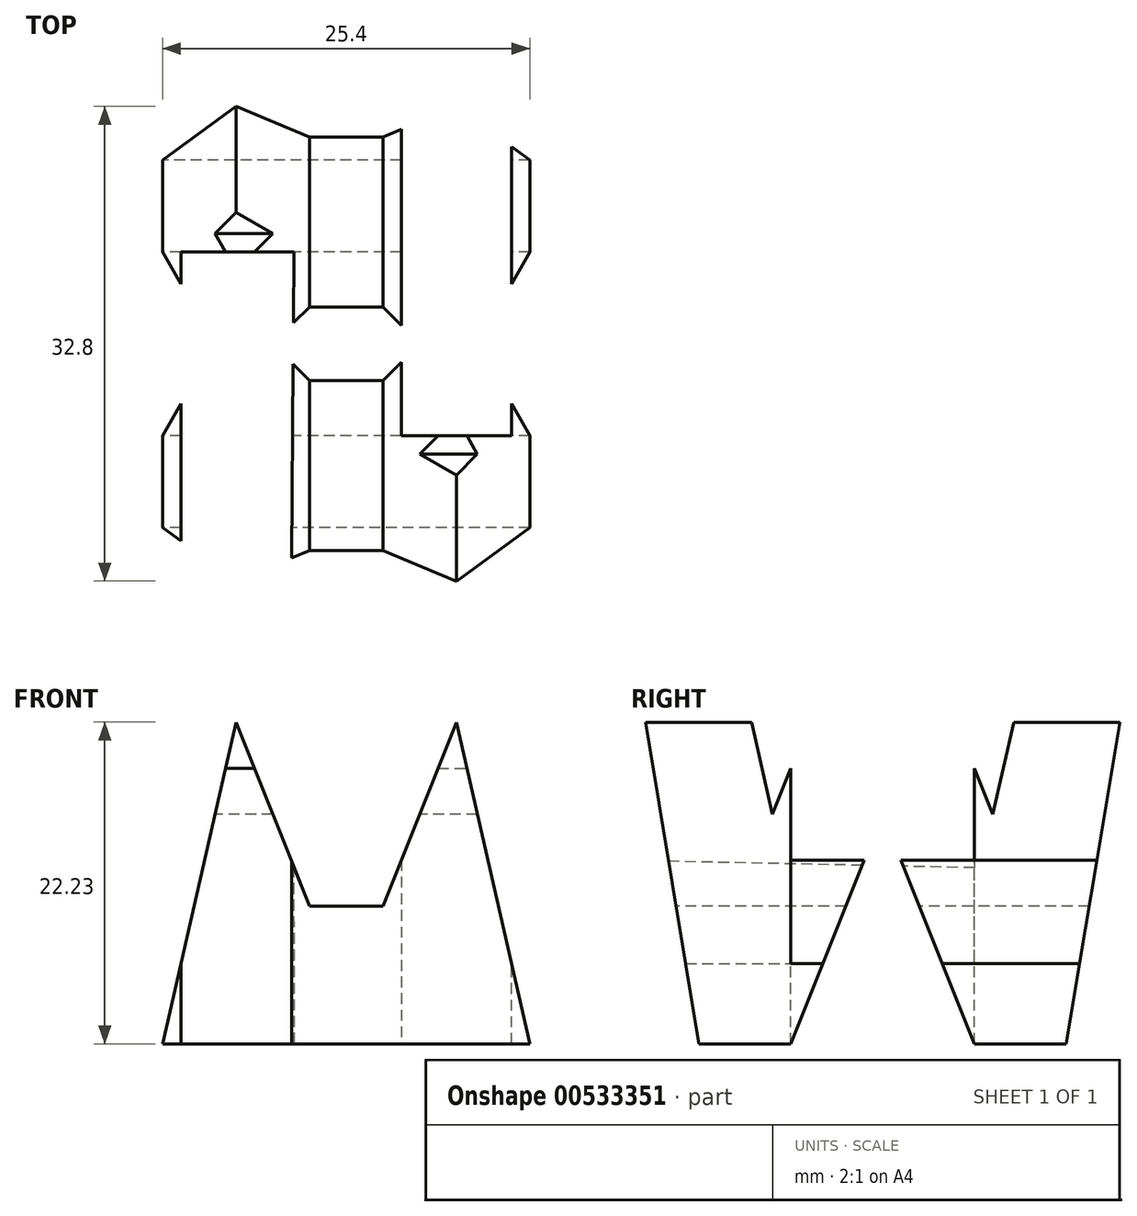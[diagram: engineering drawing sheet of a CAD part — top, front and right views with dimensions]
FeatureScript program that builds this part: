
annotation { "Feature Type Name" : "Feature", "Feature Type Description" : "" }
export const myFeature = defineFeature(function(context is Context, id is Id, definition is map)
    precondition{}
    {
        {
            var Q0;
            Q0=qCreatedBy(makeId("Front.planeOp"),FACE);
            var sketch = newSketch(context, id + "F0", { "sketchPlane" : qUnion([Q0])});
            skLineSegment(sketch, "E0", {"start": v(0, 0) * mm, "end": v(-38.1, 0) * mm});
            skLineSegment(sketch, "E1", {"start": v(-38.1, 0) * mm, "end": v(-38.1, -38.1) * mm});
            skLineSegment(sketch, "E2", {"start": v(-38.1, -38.1) * mm, "end": v(0, -38.1) * mm});
            skLineSegment(sketch, "E3", {"start": v(0, -38.1) * mm, "end": v(0, 0) * mm});
            skSolve(sketch);
        }
        {
            var Q0;
            Q0 = qSketchRegion(id + "F0", true);
            extrude(context, id + "F1", {"entities" : qUnion([Q0]), "depth" : 38.1 * mm, "offsetDistance" : 25.4 * mm});
        }
        {
            var Q0;
            Q0=qCreatedBy(makeId("Front.planeOp"),FACE);
            cPlane(context, id + "F2", {"entities" : qUnion([Q0]), "cplaneType" : CPlaneType.OFFSET, "offset" : 38.1 * mm, "width" : 152.4 * mm, "height" : 152.4 * mm});
        }
        {
            var Q0;
            Q0=qCreatedBy(makeId("Right.planeOp"),FACE);
            cPlane(context, id + "F3", {"entities" : qUnion([Q0]), "cplaneType" : CPlaneType.OFFSET, "offset" : 38.1 * mm, "oppositeDirection" : true, "width" : 152.4 * mm, "height" : 152.4 * mm});
        }
        {
            var Q0;
            Q0=qCreatedBy(id+"F3.planeOp",FACE);
            var sketch = newSketch(context, id + "F4", { "sketchPlane" : qUnion([Q0])});
            skLineSegment(sketch, "E4", {"start": v(0, 0) * mm, "end": v(-38.1, 0) * mm});
            skLineSegment(sketch, "E5", {"start": v(-38.1, 0) * mm, "end": v(-38.1, -38.1) * mm});
            skLineSegment(sketch, "E6", {"start": v(-38.1, -38.1) * mm, "end": v(0, -38.1) * mm});
            skLineSegment(sketch, "E7", {"start": v(0, -38.1) * mm, "end": v(0, 0) * mm});
            skLineSegment(sketch, "E8", {"start": v(-38.1, 0) * mm, "end": v(-31.75, -38.1) * mm});
            skLineSegment(sketch, "E9", {"start": v(-31.75, -38.1) * mm, "end": v(-25.4, -38.1) * mm});
            skLineSegment(sketch, "E10", {"start": v(-25.4, -38.1) * mm, "end": v(-19.05, -22.23) * mm});
            skLineSegment(sketch, "E11", {"start": v(-19.05, -22.23) * mm, "end": v(-12.7, -38.1) * mm});
            skLineSegment(sketch, "E12", {"start": v(-12.7, -38.1) * mm, "end": v(-6.35, -38.1) * mm});
            skLineSegment(sketch, "E13", {"start": v(-6.35, -38.1) * mm, "end": v(0, 0) * mm});
            skLineSegment(sketch, "E14", {"start": v(-31.75, 0) * mm, "end": v(-26.67, -22.23) * mm});
            skLineSegment(sketch, "E15", {"start": v(-26.67, -22.23) * mm, "end": v(-21.59, -9.52) * mm});
            skLineSegment(sketch, "E16", {"start": v(-21.59, -9.52) * mm, "end": v(-16.5, -9.52) * mm});
            skLineSegment(sketch, "E17", {"start": v(-16.5, -9.52) * mm, "end": v(-11.43, -22.23) * mm});
            skLineSegment(sketch, "E18", {"start": v(-11.43, -22.23) * mm, "end": v(-6.35, 0) * mm});
            skSolve(sketch);
        }
        {
            var Q0;
            {var subQ0=sQuery(id+"F4.wireOp",EDGE,"E10");Q0=makeQuery(id+"F4.imprint","IMPRINT",FACE,{"disambiguationData":[TD([[makeQuery(id+"F4.imprint","IMPRINT",EDGE,{"derivedFrom":subQ0}),-1.0]])]});}
            var Q1;
            {var subQ0=sQuery(id+"F4.wireOp",EDGE,"E14");Q1=makeQuery(id+"F4.imprint","IMPRINT",FACE,{"disambiguationData":[TD([[makeQuery(id+"F4.imprint","IMPRINT",EDGE,{"derivedFrom":subQ0}),1.0]])]});}
            var Q2;
            {var subQ0=sQuery(id+"F4.wireOp",EDGE,"E5");Q2=makeQuery(id+"F4.imprint","IMPRINT",FACE,{"disambiguationData":[TD([[makeQuery(id+"F4.imprint","IMPRINT",EDGE,{"derivedFrom":subQ0}),1.0]])]});}
            var Q3;
            {var subQ0=sQuery(id+"F4.wireOp",EDGE,"E7");Q3=makeQuery(id+"F4.imprint","IMPRINT",FACE,{"disambiguationData":[TD([[makeQuery(id+"F4.imprint","IMPRINT",EDGE,{"derivedFrom":subQ0}),1.0]])]});}
            extrude(context, id + "F5", {"entities" : qUnion([Q0, Q1, Q2, Q3]), "operationType" : NewBodyOperationType.REMOVE, "depth" : 38.1 * mm, "offsetDistance" : 25.4 * mm});
        }
        {
            var Q0;
            Q0=qCreatedBy(id+"F2.planeOp",FACE);
            var sketch = newSketch(context, id + "F6", { "sketchPlane" : qUnion([Q0])});
            skLineSegment(sketch, "E19", {"start": v(-38.1, -38.1) * mm, "end": v(-38.1, 0) * mm});
            skLineSegment(sketch, "E20", {"start": v(-38.1, 0) * mm, "end": v(0, 0) * mm});
            skLineSegment(sketch, "E21", {"start": v(0, 0) * mm, "end": v(0, -38.1) * mm});
            skLineSegment(sketch, "E22", {"start": v(0, -38.1) * mm, "end": v(-38.1, -38.1) * mm});
            skLineSegment(sketch, "E23", {"start": v(-38.1, -38.1) * mm, "end": v(-31.75, 0) * mm});
            skLineSegment(sketch, "E24", {"start": v(-31.75, 0) * mm, "end": v(-25.4, 0) * mm});
            skLineSegment(sketch, "E25", {"start": v(-25.4, 0) * mm, "end": v(-19.05, -15.88) * mm});
            skLineSegment(sketch, "E26", {"start": v(-19.05, -15.88) * mm, "end": v(-12.7, 0) * mm});
            skLineSegment(sketch, "E27", {"start": v(-12.7, 0) * mm, "end": v(-6.35, 0) * mm});
            skLineSegment(sketch, "E28", {"start": v(-6.35, 0) * mm, "end": v(0, -38.1) * mm});
            skLineSegment(sketch, "E29", {"start": v(-38.1, -38.1) * mm, "end": v(-31.75, -38.1) * mm});
            skLineSegment(sketch, "E30", {"start": v(-31.75, -38.1) * mm, "end": v(-38.1, -38.1) * mm});
            skLineSegment(sketch, "E31", {"start": v(-31.75, -38.1) * mm, "end": v(-26.67, -15.88) * mm});
            skLineSegment(sketch, "E32", {"start": v(-6.35, -38.1) * mm, "end": v(0, -38.1) * mm});
            skLineSegment(sketch, "E33", {"start": v(-26.67, -15.88) * mm, "end": v(-21.6, -28.58) * mm});
            skLineSegment(sketch, "E34", {"start": v(-11.43, -15.88) * mm, "end": v(-16.51, -28.58) * mm});
            skLineSegment(sketch, "E35", {"start": v(-16.51, -28.58) * mm, "end": v(-21.59, -28.58) * mm});
            skLineSegment(sketch, "E36", {"start": v(-11.43, -15.88) * mm, "end": v(-6.35, -38.1) * mm});
            skSolve(sketch);
        }
        {
            var Q0;
            Q0=makeQuery(id+"F6.imprint","IMPRINT",FACE,{"disambiguationData":[TD([[makeQuery(id+"F6.imprint","IMPRINT",EDGE,{"derivedFrom":sQuery(id+"F6.wireOp",EDGE,"E22")}),-1.0]])]});
            var Q1;
            {var subQ0=sQuery(id+"F6.wireOp",EDGE,"E25");Q1=makeQuery(id+"F6.imprint","IMPRINT",FACE,{"disambiguationData":[TD([[makeQuery(id+"F6.imprint","IMPRINT",EDGE,{"derivedFrom":subQ0}),1.0]])]});}
            var Q2;
            {var subQ0=sQuery(id+"F6.wireOp",EDGE,"E21");Q2=makeQuery(id+"F6.imprint","IMPRINT",FACE,{"disambiguationData":[TD([[makeQuery(id+"F6.imprint","IMPRINT",EDGE,{"derivedFrom":subQ0}),-1.0]])]});}
            var Q3;
            {var subQ0=sQuery(id+"F6.wireOp",EDGE,"E19");Q3=makeQuery(id+"F6.imprint","IMPRINT",FACE,{"disambiguationData":[TD([[makeQuery(id+"F6.imprint","IMPRINT",EDGE,{"derivedFrom":subQ0}),-1.0]])]});}
            extrude(context, id + "F7", {"entities" : qUnion([Q0, Q1, Q2, Q3]), "operationType" : NewBodyOperationType.REMOVE, "oppositeDirection" : true, "depth" : 38.1 * mm, "offsetDistance" : 25.4 * mm});
        }
        {
            var Q0;
            Q0=qCreatedBy(makeId("Top.planeOp"),FACE);
            var sketch = newSketch(context, id + "F8", { "sketchPlane" : qUnion([Q0])});
            skLineSegment(sketch, "E37", {"start": v(0, 0) * mm, "end": v(-38.1, 0) * mm});
            skLineSegment(sketch, "E38", {"start": v(-38.1, 0) * mm, "end": v(-38.1, -38.1) * mm});
            skLineSegment(sketch, "E39", {"start": v(-38.1, -38.1) * mm, "end": v(0, -38.1) * mm});
            skLineSegment(sketch, "E40", {"start": v(0, -38.1) * mm, "end": v(0, 0) * mm});
            skLineSegment(sketch, "E41", {"start": v(-7.62, -25.4) * mm, "end": v(-7.62, 0) * mm});
            skLineSegment(sketch, "E42", {"start": v(-7.62, 0) * mm, "end": v(-15.24, 0) * mm});
            skLineSegment(sketch, "E43", {"start": v(-15.24, 0) * mm, "end": v(-15.24, -25.4) * mm});
            skLineSegment(sketch, "E44", {"start": v(-15.24, -25.4) * mm, "end": v(-7.62, -25.4) * mm});
            skLineSegment(sketch, "E45", {"start": v(-22.65, -12.7) * mm, "end": v(-30.48, -12.7) * mm});
            skLineSegment(sketch, "E46", {"start": v(-30.48, -12.7) * mm, "end": v(-30.48, -38.1) * mm});
            skLineSegment(sketch, "E47", {"start": v(-30.48, -38.1) * mm, "end": v(-22.86, -38.1) * mm});
            skLineSegment(sketch, "E48", {"start": v(-22.86, -38.1) * mm, "end": v(-22.65, -12.7) * mm});
            skSolve(sketch);
        }
        {
            var Q0;
            Q0=makeQuery(id+"F8.imprint","IMPRINT",FACE,{"disambiguationData":[TD([[makeQuery(id+"F8.imprint","IMPRINT",EDGE,{"derivedFrom":sQuery(id+"F8.wireOp",EDGE,"E41")}),1.0]])]});
            var Q1;
            Q1=makeQuery(id+"F8.imprint","IMPRINT",FACE,{"disambiguationData":[TD([[makeQuery(id+"F8.imprint","IMPRINT",EDGE,{"derivedFrom":sQuery(id+"F8.wireOp",EDGE,"E45")}),1.0]])]});
            extrude(context, id + "F9", {"entities" : qUnion([Q0, Q1]), "operationType" : NewBodyOperationType.REMOVE, "oppositeDirection" : true, "depth" : 38.1 * mm, "offsetDistance" : 25.4 * mm});
        }
    });
